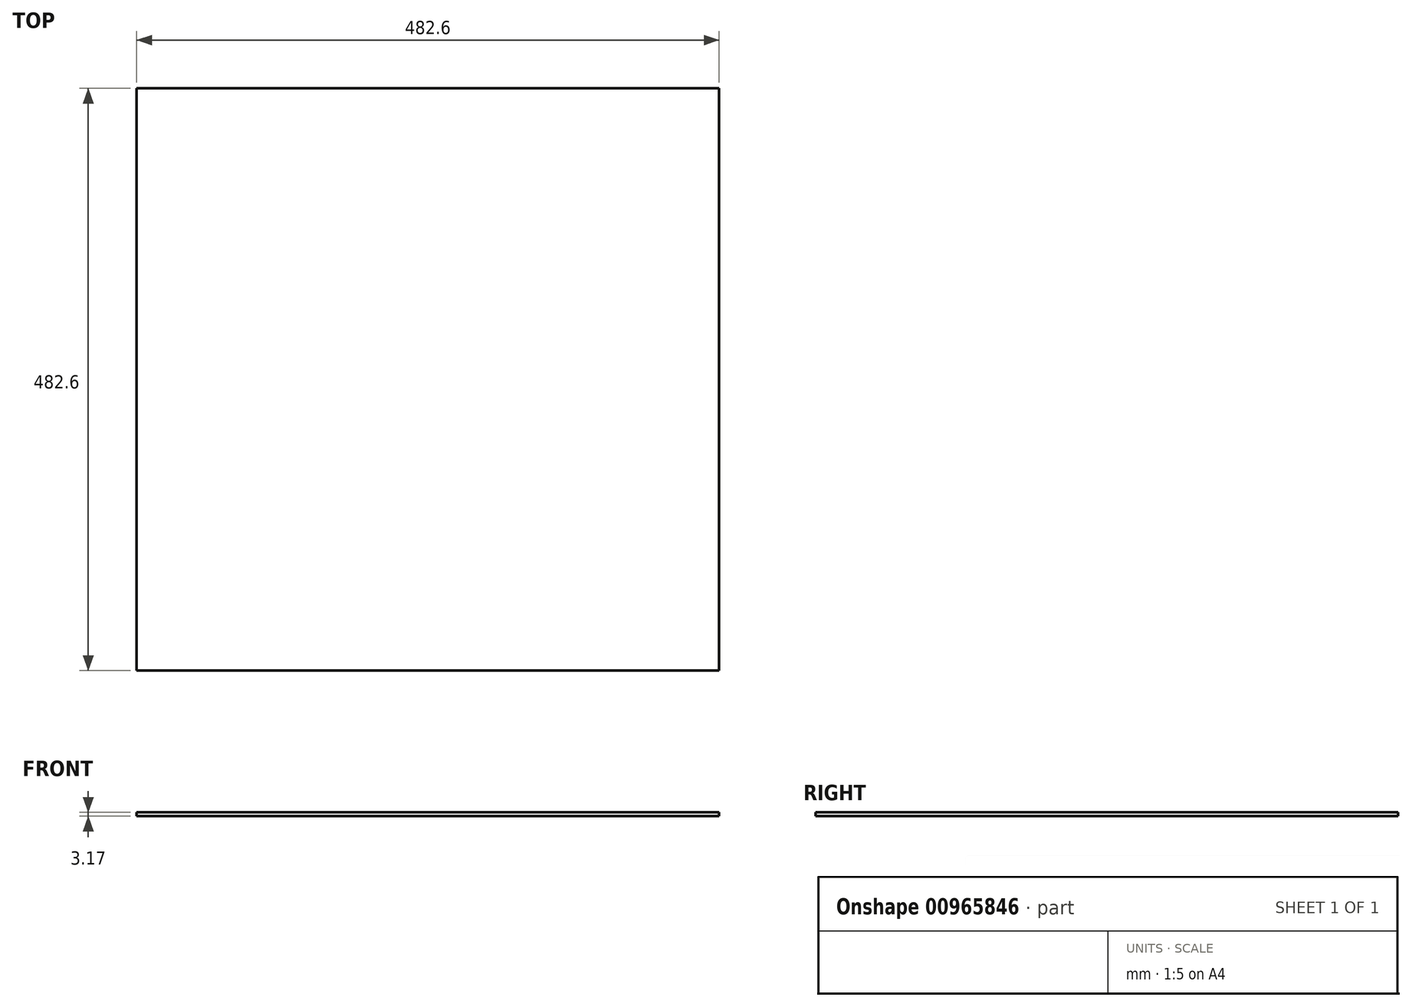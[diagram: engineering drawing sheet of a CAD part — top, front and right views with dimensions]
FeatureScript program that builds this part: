
annotation { "Feature Type Name" : "Feature", "Feature Type Description" : "" }
export const myFeature = defineFeature(function(context is Context, id is Id, definition is map)
    precondition{}
    {
        {
            var Q0;
            Q0=qCreatedBy(makeId("Top.planeOp"),FACE);
            var sketch = newSketch(context, id + "F0", { "sketchPlane" : qUnion([Q0])});
            skLineSegment(sketch, "E0.bottom", {"start": v(-258.08, 355.92) * mm, "end": v(224.52, 355.92) * mm});
            skLineSegment(sketch, "E0.top", {"start": v(-258.08, -126.68) * mm, "end": v(224.52, -126.68) * mm});
            skLineSegment(sketch, "E0.left", {"start": v(-258.08, 355.92) * mm, "end": v(-258.08, -126.68) * mm});
            skLineSegment(sketch, "E0.right", {"start": v(224.52, 355.92) * mm, "end": v(224.52, -126.68) * mm});
            skSolve(sketch);
        }
        {
            var Q0;
            Q0=makeQuery(id+"F0.imprint","IMPRINT",FACE,{"disambiguationData":[TD([[makeQuery(id+"F0.imprint","IMPRINT",EDGE,{"derivedFrom":sQuery(id+"F0.wireOp",EDGE,"E0.bottom")}),-1.0]])]});
            extrude(context, id + "F1", {"entities" : qUnion([Q0]), "depth" : 3.17 * mm, "offsetDistance" : 25.4 * mm});
        }
    });
